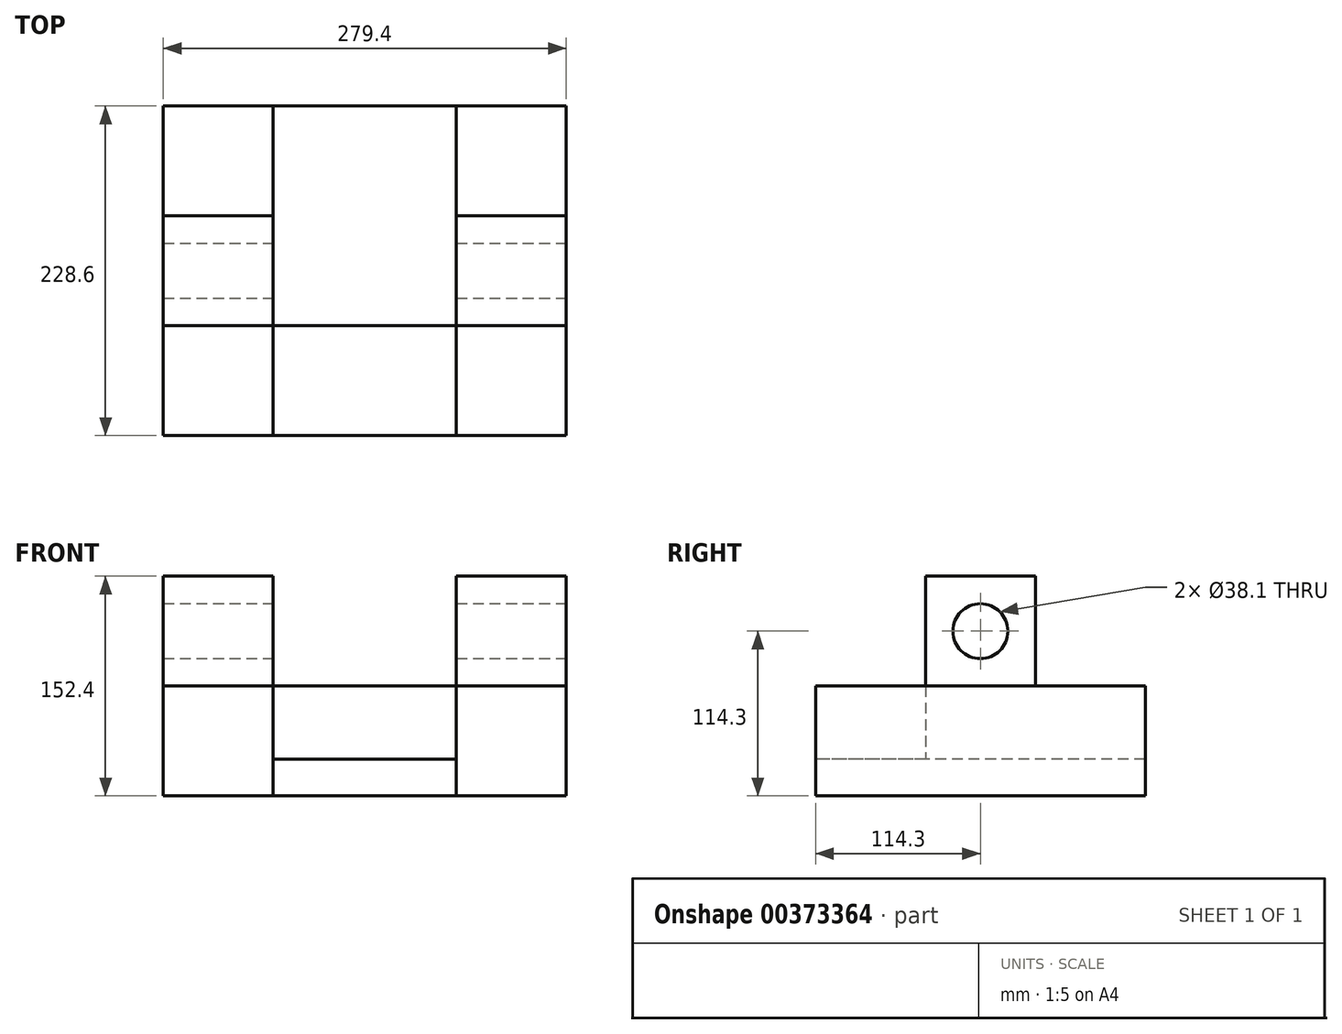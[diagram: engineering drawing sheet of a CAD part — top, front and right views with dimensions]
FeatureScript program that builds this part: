
annotation { "Feature Type Name" : "Feature", "Feature Type Description" : "" }
export const myFeature = defineFeature(function(context is Context, id is Id, definition is map)
    precondition{}
    {
        {
            var Q0;
            Q0=qCreatedBy(makeId("Top.planeOp"),FACE);
            var sketch = newSketch(context, id + "F0", { "sketchPlane" : qUnion([Q0])});
            skLineSegment(sketch, "E0.bottom", {"start": v(-63.5, 114.3) * mm, "end": v(63.5, 114.3) * mm});
            skLineSegment(sketch, "E0.top", {"start": v(-63.5, -114.3) * mm, "end": v(63.5, -114.3) * mm});
            skLineSegment(sketch, "E0.left", {"start": v(-63.5, 114.3) * mm, "end": v(-63.5, -114.3) * mm});
            skLineSegment(sketch, "E0.right", {"start": v(63.5, 114.3) * mm, "end": v(63.5, -114.3) * mm});
            skPoint(sketch, "E0.middle", {"position": v(0, 0) * mm});
            skLineSegment(sketch, "E1.bottom", {"start": v(-63.5, 114.3) * mm, "end": v(-139.7, 114.3) * mm});
            skLineSegment(sketch, "E1.top", {"start": v(-63.5, -114.3) * mm, "end": v(-139.7, -114.3) * mm});
            skLineSegment(sketch, "E1.right", {"start": v(-139.7, 114.3) * mm, "end": v(-139.7, -114.3) * mm});
            skLineSegment(sketch, "E2.bottom", {"start": v(63.5, 114.3) * mm, "end": v(139.7, 114.3) * mm});
            skLineSegment(sketch, "E2.top", {"start": v(63.5, -114.3) * mm, "end": v(139.7, -114.3) * mm});
            skLineSegment(sketch, "E2.right", {"start": v(139.7, 114.3) * mm, "end": v(139.7, -114.3) * mm});
            skSolve(sketch);
        }
        {
            var Q0;
            Q0=makeQuery(id+"F0.imprint","IMPRINT",FACE,{"disambiguationData":[TD([[makeQuery(id+"F0.imprint","IMPRINT",EDGE,{"derivedFrom":sQuery(id+"F0.wireOp",EDGE,"E1.bottom")}),1.0]])]});
            var Q1;
            Q1=makeQuery(id+"F0.imprint","IMPRINT",FACE,{"disambiguationData":[TD([[makeQuery(id+"F0.imprint","IMPRINT",EDGE,{"derivedFrom":sQuery(id+"F0.wireOp",EDGE,"E2.bottom")}),-1.0]])]});
            extrude(context, id + "F1", {"entities" : qUnion([Q0, Q1]), "depth" : 76.2 * mm});
        }
        {
            var Q0;
            Q0=makeQuery(id+"F0.imprint","IMPRINT",FACE,{"disambiguationData":[TD([[makeQuery(id+"F0.imprint","IMPRINT",EDGE,{"derivedFrom":sQuery(id+"F0.wireOp",EDGE,"E0.bottom")}),-1.0]])]});
            extrude(context, id + "F2", {"entities" : qUnion([Q0]), "depth" : 25.4 * mm});
        }
        {
            var Q0;
            Q0=makeQuery(id+"F2.opExtrude","CAP_FACE",FACE,{"disambiguationData":[OSD([sQuery(id+"F0.wireOp",EDGE,"E0.bottom"),sQuery(id+"F0.wireOp",EDGE,"E0.top"),sQuery(id+"F0.wireOp",EDGE,"E0.left"),sQuery(id+"F0.wireOp",EDGE,"E0.right")])],"isStart":false});
            var sketch = newSketch(context, id + "F3", { "sketchPlane" : qUnion([Q0])});
            skLineSegment(sketch, "E3.bottom", {"start": v(-63.5, -114.3) * mm, "end": v(63.5, -114.3) * mm});
            skLineSegment(sketch, "E3.top", {"start": v(-63.5, -38.1) * mm, "end": v(63.5, -38.1) * mm});
            skLineSegment(sketch, "E3.left", {"start": v(-63.5, -114.3) * mm, "end": v(-63.5, -38.1) * mm});
            skLineSegment(sketch, "E3.right", {"start": v(63.5, -114.3) * mm, "end": v(63.5, -38.1) * mm});
            skSolve(sketch);
        }
        {
            var Q0;
            Q0 = qSketchRegion(id + "F3", true);
            extrude(context, id + "F4", {"entities" : qUnion([Q0]), "depth" : 50.8 * mm});
        }
        {
            var Q0;
            Q0=makeQuery(id+"F1.opExtrude","CAP_FACE",FACE,{"disambiguationData":[OSD([sQuery(id+"F0.wireOp",EDGE,"E1.bottom"),sQuery(id+"F0.wireOp",EDGE,"E1.top"),sQuery(id+"F0.wireOp",EDGE,"E0.left"),sQuery(id+"F0.wireOp",EDGE,"E1.right")])],"isStart":false});
            var sketch = newSketch(context, id + "F5", { "sketchPlane" : qUnion([Q0])});
            skLineSegment(sketch, "E4.bottom", {"start": v(-139.7, 38.1) * mm, "end": v(-63.5, 38.1) * mm});
            skLineSegment(sketch, "E4.top", {"start": v(-139.7, -38.1) * mm, "end": v(-63.5, -38.1) * mm});
            skLineSegment(sketch, "E4.left", {"start": v(-139.7, 38.1) * mm, "end": v(-139.7, -38.1) * mm});
            skLineSegment(sketch, "E4.right", {"start": v(-63.5, 38.1) * mm, "end": v(-63.5, -38.1) * mm});
            skPoint(sketch, "E4.middle", {"position": v(-101.6, 0) * mm});
            skSolve(sketch);
        }
        {
            var Q0;
            Q0=makeQuery(id+"F1.opExtrude","CAP_FACE",FACE,{"disambiguationData":[OSD([sQuery(id+"F0.wireOp",EDGE,"E2.bottom"),sQuery(id+"F0.wireOp",EDGE,"E2.top"),sQuery(id+"F0.wireOp",EDGE,"E0.right"),sQuery(id+"F0.wireOp",EDGE,"E2.right")])],"isStart":false});
            var sketch = newSketch(context, id + "F6", { "sketchPlane" : qUnion([Q0])});
            skLineSegment(sketch, "E5.bottom", {"start": v(63.5, 38.1) * mm, "end": v(139.7, 38.1) * mm});
            skLineSegment(sketch, "E5.top", {"start": v(63.5, -38.1) * mm, "end": v(139.7, -38.1) * mm});
            skLineSegment(sketch, "E5.left", {"start": v(63.5, 38.1) * mm, "end": v(63.5, -38.1) * mm});
            skLineSegment(sketch, "E5.right", {"start": v(139.7, 38.1) * mm, "end": v(139.7, -38.1) * mm});
            skPoint(sketch, "E5.middle", {"position": v(101.6, 0) * mm});
            skSolve(sketch);
        }
        {
            var Q0;
            Q0=makeQuery(id+"F5.imprint","IMPRINT",FACE,{"disambiguationData":[TD([[makeQuery(id+"F5.imprint","IMPRINT",EDGE,{"derivedFrom":sQuery(id+"F5.wireOp",EDGE,"E4.bottom")}),-1.0]])]});
            var Q1;
            Q1=makeQuery(id+"F6.imprint","IMPRINT",FACE,{"disambiguationData":[TD([[makeQuery(id+"F6.imprint","IMPRINT",EDGE,{"derivedFrom":sQuery(id+"F6.wireOp",EDGE,"E5.bottom")}),-1.0]])]});
            extrude(context, id + "F7", {"entities" : qUnion([Q0, Q1]), "depth" : 76.2 * mm});
        }
        {
            var Q0;
            Q0=makeQuery(id+"F7.opExtrude","SWEPT_FACE",FACE,{"disambiguationData":[OSD([sQuery(id+"F6.wireOp",EDGE,"E5.right")])]});
            var sketch = newSketch(context, id + "F8", { "sketchPlane" : qUnion([Q0])});
            skCircle(sketch, "E6", {"center": v(0, 114.3) * mm, "radius": 19.05 * mm});
            skSolve(sketch);
        }
        {
            var Q0;
            Q0=sQuery(id+"F8.wireOp",VERTEX,"E6.center");
            var Q1;
            Q1=makeQuery(id+"F7.opExtrude","SWEPT_BODY",BODY,{"disambiguationData":[OSD([sQuery(id+"F5.wireOp",EDGE,"E4.bottom"),sQuery(id+"F5.wireOp",EDGE,"E4.top"),sQuery(id+"F5.wireOp",EDGE,"E4.left"),sQuery(id+"F5.wireOp",EDGE,"E4.right")])]});
            var Q2;
            Q2=makeQuery(id+"F7.opExtrude","SWEPT_BODY",BODY,{"disambiguationData":[OSD([sQuery(id+"F6.wireOp",EDGE,"E5.bottom"),sQuery(id+"F6.wireOp",EDGE,"E5.top"),sQuery(id+"F6.wireOp",EDGE,"E5.left"),sQuery(id+"F6.wireOp",EDGE,"E5.right")])]});
            hole(context, id + "F9", {"style" : HoleStyle.SIMPLE, "endStyle" : HoleEndStyle.THROUGH, "holeDiameter" : 38.1 * mm, "isTappedThrough" : true, "tappedDepth" : 12.7 * mm, "tapClearance" : 3, "locations" : qUnion([Q0]), "scope" : qUnion([Q1, Q2])});
        }
    });
